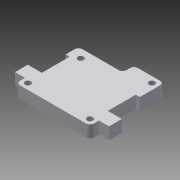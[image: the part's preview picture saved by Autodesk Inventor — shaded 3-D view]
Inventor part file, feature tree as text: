
AUTODESK INVENTOR PART (.ipt)
format: ipt  version: 2013 (Build 170138000, 138)  size: 110,592 bytes
history: native  units: mm
features: extrude x1, sketch x1
ambient origin geometry x8: Origin, YZ Plane, XZ Plane, XY Plane, X Axis, Y Axis, Z Axis, Center Point
bodies: Solid1 (feature_tree)
feature tree (2):
  extrude  "Extrusion1"  [1 undecoded]
  sketch  "Sketch1"  dims[d0=6.0mm d1=0.0mm]
note: 1 required parameter value undecoded (feature->parameter linkage not recoverable at this tier; creation-order binding heuristic only, values carry confidence <= 0.55)
